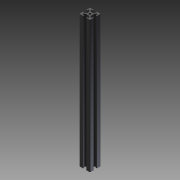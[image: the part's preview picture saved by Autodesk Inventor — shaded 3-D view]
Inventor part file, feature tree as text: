
AUTODESK INVENTOR PART (.ipt)
format: ipt  version: 2014 SP1 (Build 180222100, 222)  size: 172,544 bytes
history: native  units: mm
features: other x7, sketch x2, extrude x1, revolve x1
ambient origin geometry x8: Origin, YZ Plane, XZ Plane, XY Plane, X Axis, Y Axis, Z Axis, Center Point
bodies: Solid1 (feature_tree)
feature tree (11):
  extrude  "Extrusion1"  TaperAngle=360.0deg  [1 undecoded]
  revolve  "Revolution1"  [1 undecoded]
  other  "C1_XY"
  other  "C1_YZ"
  other  "C1_ZX"
  other  "C1_X"
  other  "C1_Y"
  other  "C1_Z"
  other  "C1_Center"
  sketch  "Sketch_1"  dims[d0=250.0mm d1=0.0mm d2=360.0deg]
  sketch  "Sketch_2"
note: 2 required parameter values undecoded (feature->parameter linkage not recoverable at this tier; creation-order binding heuristic only, values carry confidence <= 0.55)
